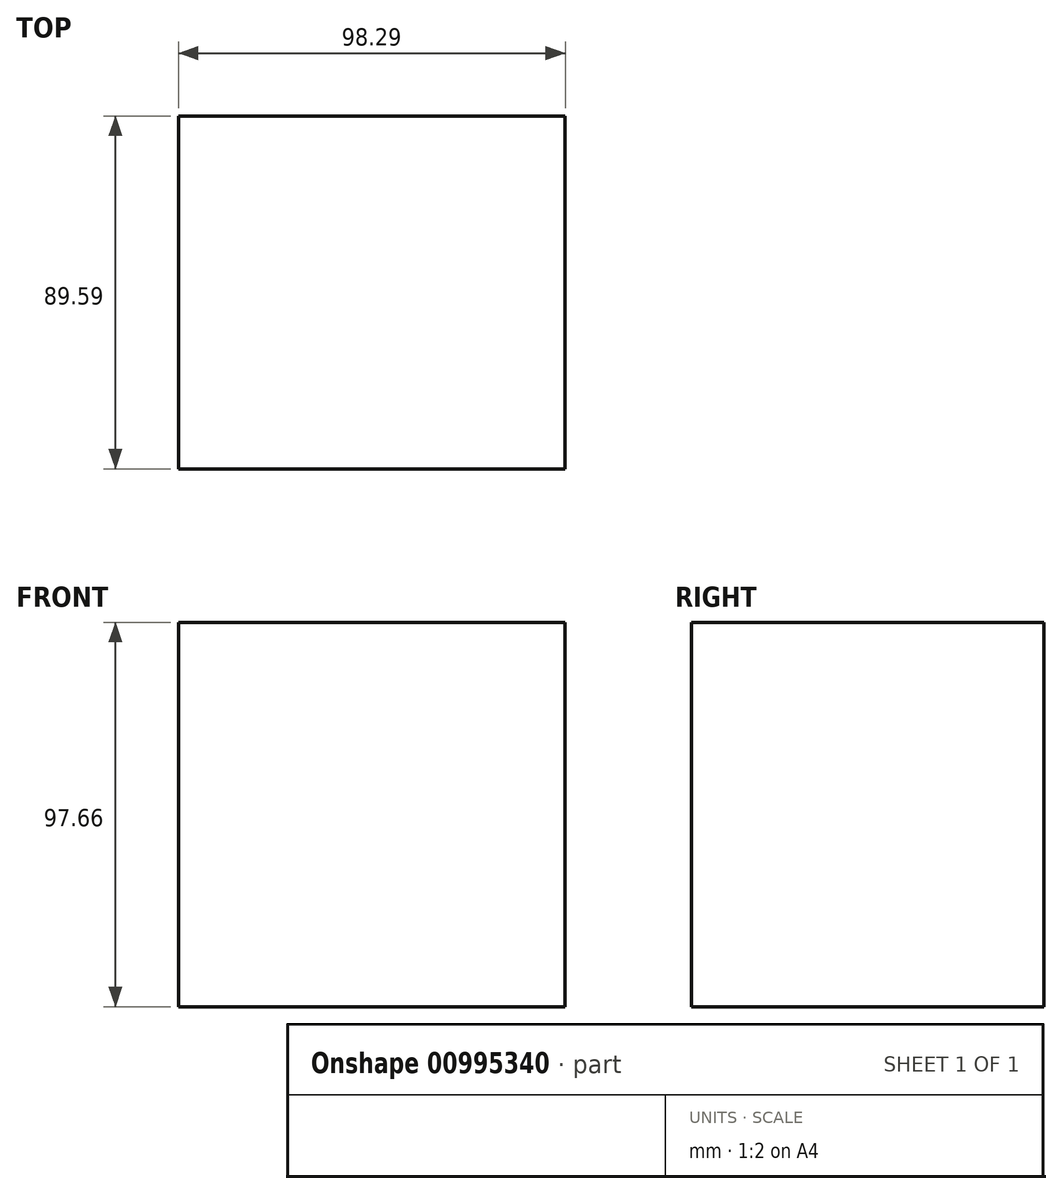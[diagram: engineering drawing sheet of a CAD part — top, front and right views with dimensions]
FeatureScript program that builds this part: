
annotation { "Feature Type Name" : "Feature", "Feature Type Description" : "" }
export const myFeature = defineFeature(function(context is Context, id is Id, definition is map)
    precondition{}
    {
        {
            var Q0;
            Q0=qCreatedBy(makeId("Front.planeOp"),FACE);
            var sketch = newSketch(context, id + "F0", { "sketchPlane" : qUnion([Q0])});
            skLineSegment(sketch, "E0.bottom", {"start": v(0, 0) * mm, "end": v(98.29, 0) * mm});
            skLineSegment(sketch, "E0.top", {"start": v(0, 97.66) * mm, "end": v(98.29, 97.66) * mm});
            skLineSegment(sketch, "E0.left", {"start": v(0, 0) * mm, "end": v(0, 97.66) * mm});
            skLineSegment(sketch, "E0.right", {"start": v(98.29, 0) * mm, "end": v(98.29, 97.66) * mm});
            skSolve(sketch);
        }
        {
            var Q0;
            Q0=makeQuery(id+"F0.imprint","IMPRINT",FACE,{"disambiguationData":[TD([[makeQuery(id+"F0.imprint","IMPRINT",EDGE,{"derivedFrom":sQuery(id+"F0.wireOp",EDGE,"E0.bottom")}),1.0]])]});
            extrude(context, id + "F1", {"entities" : qUnion([Q0]), "depth" : 89.6 * mm, "offsetDistance" : 25.4 * mm});
        }
    });
